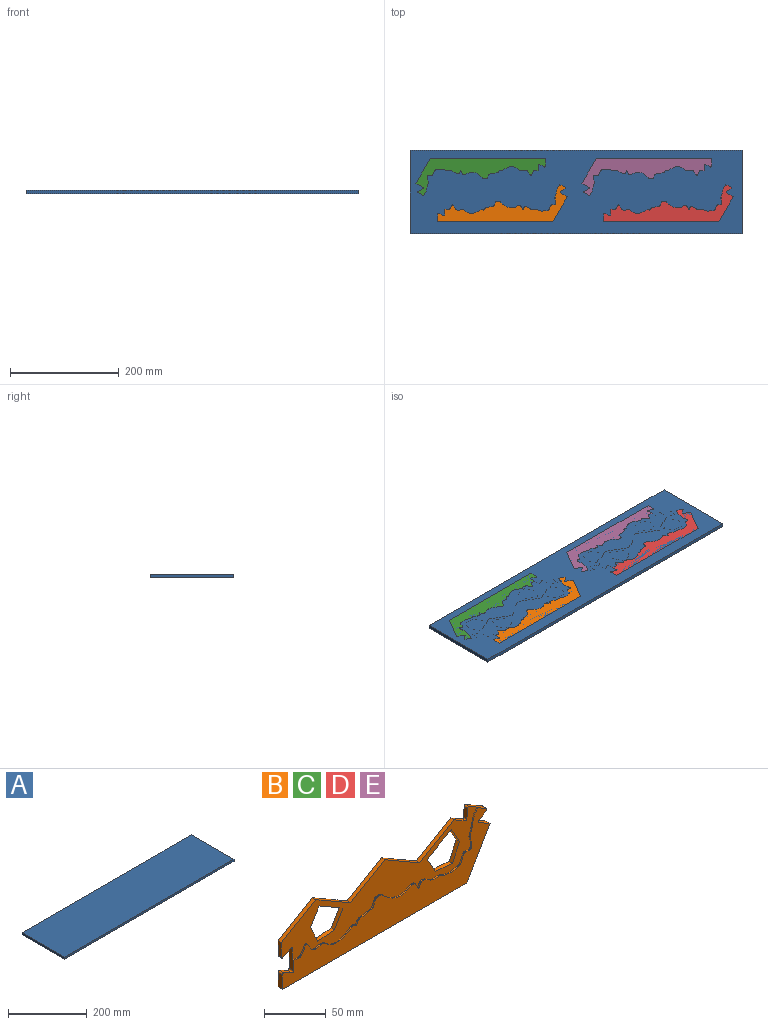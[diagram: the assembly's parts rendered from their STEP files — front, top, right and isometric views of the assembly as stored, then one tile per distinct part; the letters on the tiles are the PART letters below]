
ASSEMBLY  parts=5 mates=2
PART A: 6 faces, bbox 609.6x152.4x6.4 mm
  f0: plane 152.4x6.35mm, normal (1,0,0), area 967.7mm2, adj f1,f3,f4,f5
  f1: plane 609.6x6.35mm, normal (0,1,0), area 3871mm2, adj f0,f2,f4,f5
  f2: plane 152.4x6.35mm, normal (-1,0,0), area 967.7mm2, adj f1,f3,f4,f5
  f3: plane 609.6x6.35mm, normal (0,-1,0), area 3871mm2, adj f0,f2,f4,f5
  f4: plane 609.6x152.4mm, normal (0,0,1), area 92903mm2, adj f0,f1,f2,f3
  f5: plane 609.6x152.4mm, normal (0,0,-1), area 92903mm2, adj f0,f1,f2,f3
PART B: 40 faces, bbox 238.1x5.1x73.8 mm
  f0: plane 238.12x73.77mm, normal (0,1,0), area 11450.1mm2, adj f2,f3,f4,f5,f6,f7,f8,f9
  f1: plane 224.63x59.17mm, normal (0,-1,0), area 5573.3mm2, adj f2,f3,f4,f5,f6,f7,f8,f9
  f2: plane 18.44x10.65mm, normal (0.5,0,0.87), area 94.6mm2, adj f0,f1,f9,f26,f27,f29
  f3: plane 39.69x22.91mm, normal (-0.5,0,0.87), area 174.6mm2, adj f0,f1,f4,f16
  f4: plane 14.51x3.81mm, normal (-1,0,0), area 55.3mm2, adj f0,f1,f3,f5
  f5: cylinder r=1.27mm len=3.81mm, axis (0,1,0), area 9.8mm2, adj f0,f1,f4,f6
  f6: plane 9.02x4.51mm, normal (0.45,0,-0.89), area 38.4mm2, adj f0,f1,f5,f7
  f7: cylinder r=1.27mm len=3.81mm, axis (0,1,0), area 9.8mm2, adj f0,f1,f6,f8
  f8: plane 21.29x5.08mm, normal (-1,0,0), area 94.6mm2, adj f0,f1,f7,f17,f27,f28
  f9: cylinder r=1.27mm len=3.81mm, axis (0,1,0), area 9.8mm2, adj f0,f1,f2,f10
  f10: plane 10.07x3.81mm, normal (-1,0,0.06), area 38.4mm2, adj f0,f1,f9,f11
  f11: cylinder r=1.27mm len=3.81mm, axis (0,1,0), area 9.8mm2, adj f0,f1,f10,f12
  f12: plane 12.56x7.25mm, normal (0.5,0,0.87), area 55.3mm2, adj f0,f1,f11,f13
  f13: plane 39.69x22.91mm, normal (-0.5,0,0.87), area 174.6mm2, adj f0,f1,f12,f14
  f14: plane 39.69x22.91mm, normal (0.5,0,0.87), area 174.6mm2, adj f0,f1,f13,f15
  f15: plane 39.69x22.91mm, normal (-0.5,0,0.87), area 174.6mm2, adj f0,f1,f14,f16
  f16: plane 39.69x22.91mm, normal (0.5,0,0.87), area 174.6mm2, adj f0,f1,f3,f15
  f17: cylinder r=1.27mm len=5.08mm, axis (0,1,0), area 13.1mm2, adj f0,f8,f18,f27
  f18: plane 9.02x5.08mm, normal (0.45,0,0.89), area 51.3mm2, adj f0,f17,f19,f27
  f19: cylinder r=1.27mm len=5.08mm, axis (0,1,0), area 13.1mm2, adj f0,f18,f20,f27
  f20: plane 14.51x5.08mm, normal (-1,0,0), area 73.7mm2, adj f0,f19,f21,f27
  f21: plane 211.66x5.08mm, normal (0,0,-1), area 1075.3mm2, adj f0,f20,f22,f27
  f22: plane 45.82x26.46mm, normal (0.87,0,-0.5), area 268.8mm2, adj f0,f21,f23,f27
  f23: plane 12.56x7.25mm, normal (0.5,0,0.87), area 73.7mm2, adj f0,f22,f24,f27
  f24: cylinder r=1.27mm len=5.08mm, axis (0,1,0), area 13.1mm2, adj f0,f23,f25,f27
  f25: plane 8.42x5.56mm, normal (0.55,0,-0.83), area 51.3mm2, adj f0,f24,f26,f27
  f26: cylinder r=1.27mm len=5.08mm, axis (0,1,0), area 13.1mm2, adj f0,f2,f25,f27
  f27: plane 238.12x68.28mm, normal (0,-1,0), area 5876.9mm2, adj f2,f8,f17,f18,f19,f20,f21,f22
  f28: extruded ~188.29x22.21mm, area 275.6mm2, adj f1,f8,f27,f29
  f29: extruded ~47.41x23.63mm, area 77.2mm2, adj f1,f2,f27,f28
  f30: plane 27.5x15.88mm, normal (0.5,0,-0.87), area 121mm2, adj f0,f1,f31,f34
  f31: plane 16.78x9.69mm, normal (0.87,0,0.5), area 73.8mm2, adj f0,f1,f30,f32
  f32: plane 19.3x3.81mm, normal (0.09,0,1), area 73.8mm2, adj f0,f1,f31,f33
  f33: plane 17.56x8.2mm, normal (-0.91,0,0.42), area 73.8mm2, adj f0,f1,f32,f34
  f34: plane 16.78x9.69mm, normal (-0.87,0,-0.5), area 73.8mm2, adj f0,f1,f30,f33
  f35: plane 27.5x15.88mm, normal (-0.5,0,-0.87), area 121mm2, adj f0,f1,f36,f39
  f36: plane 16.78x9.69mm, normal (0.87,0,-0.5), area 73.8mm2, adj f0,f1,f35,f37
  f37: plane 17.56x8.2mm, normal (0.91,0,0.42), area 73.8mm2, adj f0,f1,f36,f38
  f38: plane 19.3x3.81mm, normal (-0.09,0,1), area 73.8mm2, adj f0,f1,f37,f39
  f39: plane 16.78x9.69mm, normal (-0.87,0,0.5), area 73.8mm2, adj f0,f1,f35,f38
PART C: same geometry as B
PART D: same geometry as B
PART E: same geometry as B
PLACE A t=(41.32,14.62,-200.25)mm
PLACE B rot(axis=(-1,0,0),90deg) t=(-212.69,51.63,-198.98)mm
PLACE C rot(axis=(0,-0.71,0.71),180deg) t=(-14.38,-15.35,-198.98)mm
PLACE D rot(axis=(-1,0,0),90deg) t=(92.11,51.63,-198.98)mm
PLACE E rot(axis=(0,-0.71,0.71),180deg) t=(290.42,-15.35,-198.98)mm
MATE planar C.f27 <-> A.f4  axis (0,0,1) through (-140.13,60.25,-193.9)mm
MATE planar B.f27 <-> A.f4  axis (0,0,1) through (-86.94,-23.97,-193.9)mm
